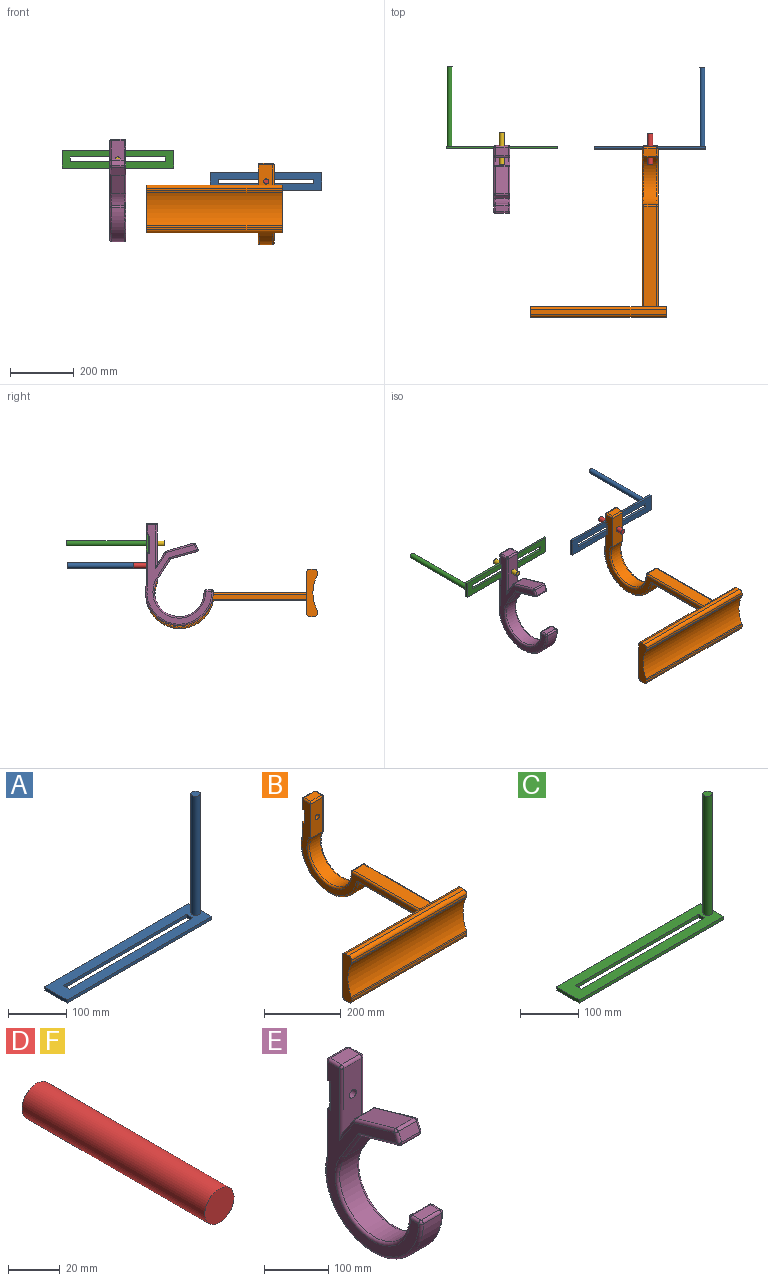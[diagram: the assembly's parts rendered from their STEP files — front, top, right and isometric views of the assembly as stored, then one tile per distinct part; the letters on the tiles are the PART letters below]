
ASSEMBLY  parts=6 mates=4
PART A: 12 faces, bbox 350x54.6x256.5 mm
  f0: plane 350x54.58mm, normal (0,0,1), area 14418.2mm2, adj f1,f3,f4,f5,f6,f7,f8,f9
  f1: plane 350x6.45mm, normal (0,-1,0), area 2257.7mm2, adj f0,f2,f4,f5
  f2: plane 350x54.58mm, normal (0,0,-1), area 14619.2mm2, adj f1,f3,f4,f5,f6,f7,f8,f9
  f3: plane 350x6.45mm, normal (0,1,0), area 2257.7mm2, adj f0,f2,f4,f5
  f4: plane 54.58x6.45mm, normal (1,0,0), area 352.1mm2, adj f0,f1,f2,f3
  f5: plane 54.58x6.45mm, normal (-1,0,0), area 352.1mm2, adj f0,f1,f2,f3
  f6: plane 15x6.45mm, normal (1,0,0), area 96.8mm2, adj f0,f2,f7,f9
  f7: plane 298.97x6.45mm, normal (0,1,0), area 1928.6mm2, adj f0,f2,f6,f8
  f8: plane 15x6.45mm, normal (-1,0,0), area 96.8mm2, adj f0,f2,f7,f9
  f9: plane 298.97x6.45mm, normal (0,-1,0), area 1928.6mm2, adj f0,f2,f6,f8
  f10: cylinder r=8mm len=250mm, axis (0,0,-1), area 12566.4mm2, adj f0,f11
  f11: plane 16x16mm, normal (0,0,1), area 201.1mm2, adj f10
PART B: 68 faces, bbox 425x547.6x264.4 mm
  f0: plane 41.08x40mm, normal (0,1,0), area 1643.3mm2, adj f29,f36,f40,f42
  f1: plane 500.7x245.65mm, normal (-1,0,0), area 13483.1mm2, adj f11,f25,f26,f28,f29,f33,f37,f39
  f2: plane 500.7x245.65mm, normal (1,0,0), area 12934.7mm2, adj f11,f25,f28,f29,f31,f32,f35,f36
  f3: cylinder r=7.5mm len=27.51mm, axis (0,-1,0), area 1296.5mm2, adj f26,f30
  f4: plane 425x7.79mm, normal (0,-1,0), area 3309mm2, adj f13,f16,f19,f22
  f5: plane 290x40mm, normal (0,0,-1), area 11600mm2, adj f11,f31,f33,f34
  f6: plane 316.33x40mm, normal (0,0,1), area 12653.2mm2, adj f11,f44,f50,f51
  f7: cylinder r=106.68mm len=210.82mm, axis (-1,0,0), area 13645.9mm2, adj f34,f35,f39,f40
  f8: cylinder r=77.9mm len=155.57mm, axis (-1,0,0), area 10978.7mm2, adj f10,f43,f48,f49
  f9: plane 40x6.31mm, normal (0,1,0), area 252.3mm2, adj f45,f48,f51,f54
  f10: plane 42.72x0.17mm, normal (0,-0.55,0.83), area 7.8mm2, adj f8,f25,f43,f49
  f11: plane 425x130mm, normal (0,1,0), area 54021.5mm2, adj f1,f2,f5,f6,f13,f16,f21,f23
  f12: plane 425x7.79mm, normal (0,-1,0), area 3309mm2, adj f13,f16,f18,f20
  f13: plane 150x33.08mm, normal (-1,0,0), area 3853.4mm2, adj f4,f11,f12,f14,f15,f17,f18,f19
  f14: plane 425x13.08mm, normal (0,0,1), area 5558.4mm2, adj f13,f16,f22,f23
  f15: plane 425x13.08mm, normal (0,0,-1), area 5558.4mm2, adj f13,f16,f20,f21
  f16: plane 150x33.08mm, normal (1,0,0), area 3853.4mm2, adj f4,f11,f12,f14,f15,f17,f18,f19
  f17: cylinder r=115.34mm len=425mm, axis (1,0,0), area 46473mm2, adj f13,f16,f18,f19
  f18: cylinder r=10mm len=425mm, axis (1,0,0), area 2014.7mm2, adj f12,f13,f16,f17
  f19: cylinder r=10mm len=425mm, axis (1,0,0), area 2014.7mm2, adj f4,f13,f16,f17
  f20: cylinder r=10mm len=425mm, axis (-1,0,0), area 6675.9mm2, adj f12,f13,f15,f16
  f21: cylinder r=10mm len=425mm, axis (1,0,0), area 6675.9mm2, adj f11,f13,f15,f16
  f22: cylinder r=10mm len=425mm, axis (1,0,0), area 6675.9mm2, adj f4,f13,f14,f16
  f23: cylinder r=10mm len=425mm, axis (-1,0,0), area 6675.9mm2, adj f11,f13,f14,f16
  f24: plane 40x26.99mm, normal (0,1,0), area 1079.5mm2, adj f56,f57,f59,f60
  f25: plane 50x6.79mm, normal (0,-0.18,-0.98), area 55.4mm2, adj f1,f2,f10,f26,f43,f49,f65
  f26: plane 109.23x45mm, normal (0,-1,0), area 4738.7mm2, adj f1,f3,f25,f63,f65
  f27: plane 40x23.43mm, normal (0,0,1), area 937.2mm2, adj f55,f60,f62,f63
  f28: plane 50x5.92mm, normal (0,0,-1), area 56.6mm2, adj f1,f2,f30,f57,f66,f67
  f29: plane 50x10.92mm, normal (0,0,1), area 295.9mm2, adj f0,f1,f2,f30,f36,f42,f66,f67
  f30: plane 40.56x40mm, normal (0,1,0), area 1445.7mm2, adj f3,f28,f29,f66,f67
  f31: cylinder r=5mm len=290mm, axis (0,-1,0), area 2277.7mm2, adj f2,f5,f11,f32
  f32: torus R=10mm, axis (1,0,0), area 72.4mm2, adj f2,f31,f34,f35
  f33: cylinder r=5mm len=290mm, axis (0,1,0), area 2277.7mm2, adj f1,f5,f11,f37
  f34: cylinder r=5mm len=40mm, axis (-1,0,0), area 270.4mm2, adj f5,f7,f32,f37
  f35: torus R=101.68mm, axis (1,0,0), area 2633.7mm2, adj f2,f7,f32,f38
  f36: cylinder r=5mm len=41.08mm, axis (0,0,-1), area 322.7mm2, adj f0,f2,f29,f38
  f37: torus R=10mm, axis (1,0,0), area 72.4mm2, adj f1,f33,f34,f39
  f38: torus R=10mm, axis (1,0,0), area 14.7mm2, adj f2,f35,f36,f40
  f39: torus R=101.68mm, axis (1,0,0), area 2633.7mm2, adj f1,f7,f37,f41
  f40: cylinder r=5mm len=40mm, axis (-1,0,0), area 55mm2, adj f0,f7,f38,f41
  f41: torus R=10mm, axis (1,0,0), area 14.7mm2, adj f1,f39,f40,f42
  f42: cylinder r=5mm len=41.08mm, axis (0,0,1), area 322.7mm2, adj f0,f1,f29,f41
  f43: torus R=82.9mm, axis (1,0,0), area 2196.5mm2, adj f1,f8,f10,f25,f46
  f44: cylinder r=5mm len=316.33mm, axis (0,-1,0), area 2484.5mm2, adj f1,f6,f11,f47
  f45: cylinder r=5mm len=6.31mm, axis (0,0,-1), area 49.5mm2, adj f1,f9,f46,f47
  f46: torus R=10mm, axis (1,0,0), area 4.1mm2, adj f1,f43,f45,f48
  f47: sphere r=5mm, area 39.3mm2, adj f44,f45,f51
  f48: cylinder r=5mm len=40mm, axis (-1,0,0), area 15.3mm2, adj f8,f9,f46,f52
  f49: torus R=82.9mm, axis (1,0,0), area 2196.5mm2, adj f2,f8,f10,f25,f52
  f50: cylinder r=5mm len=316.33mm, axis (0,1,0), area 2484.5mm2, adj f2,f6,f11,f53
  f51: cylinder r=5mm len=40mm, axis (-1,0,0), area 314.2mm2, adj f6,f9,f47,f53
  f52: torus R=10mm, axis (1,0,0), area 4.1mm2, adj f2,f48,f49,f54
  f53: sphere r=5mm, area 39.3mm2, adj f50,f51,f54
  f54: cylinder r=5mm len=6.31mm, axis (0,0,1), area 49.5mm2, adj f2,f9,f52,f53
  f55: cylinder r=5mm len=23.43mm, axis (0,1,0), area 184mm2, adj f2,f27,f58,f64
  f56: cylinder r=5mm len=31.99mm, axis (0,0,-1), area 237mm2, adj f2,f24,f57,f58
  f57: cylinder r=5mm len=50mm, axis (1,0,0), area 364.2mm2, adj f24,f28,f56,f59
  f58: sphere r=5mm, area 39.3mm2, adj f55,f56,f60
  f59: cylinder r=5mm len=31.99mm, axis (0,0,1), area 237mm2, adj f1,f24,f57,f61
  f60: cylinder r=5mm len=40mm, axis (-1,0,0), area 314.2mm2, adj f24,f27,f58,f61
  f61: sphere r=5mm, area 39.3mm2, adj f59,f60,f62
  f62: cylinder r=5mm len=28.43mm, axis (0,-1,0), area 209mm2, adj f1,f27,f61,f63
  f63: cylinder r=5mm len=45mm, axis (-1,0,0), area 339.2mm2, adj f26,f27,f62,f64
  f64: sphere r=5mm, area 39.3mm2, adj f55,f63,f65
  f65: cylinder r=5mm len=110.15mm, axis (0,0,1), area 860.5mm2, adj f2,f25,f26,f64
  f66: cylinder r=5mm len=40.56mm, axis (0,0,-1), area 318.6mm2, adj f1,f28,f29,f30
  f67: cylinder r=5mm len=40.56mm, axis (0,0,1), area 318.6mm2, adj f2,f28,f29,f30
PART C: 12 faces, bbox 350x54.6x256.5 mm
  f0: plane 350x54.58mm, normal (0,0,1), area 14418.2mm2, adj f1,f3,f4,f5,f6,f7,f8,f9
  f1: plane 350x6.45mm, normal (0,-1,0), area 2257.7mm2, adj f0,f2,f4,f5
  f2: plane 350x54.58mm, normal (0,0,-1), area 14619.2mm2, adj f1,f3,f4,f5,f6,f7,f8,f9
  f3: plane 350x6.45mm, normal (0,1,0), area 2257.7mm2, adj f0,f2,f4,f5
  f4: plane 54.58x6.45mm, normal (1,0,0), area 352.1mm2, adj f0,f1,f2,f3
  f5: plane 54.58x6.45mm, normal (-1,0,0), area 352.1mm2, adj f0,f1,f2,f3
  f6: plane 15x6.45mm, normal (1,0,0), area 96.8mm2, adj f0,f2,f7,f9
  f7: plane 298.97x6.45mm, normal (0,1,0), area 1928.6mm2, adj f0,f2,f6,f8
  f8: plane 15x6.45mm, normal (-1,0,0), area 96.8mm2, adj f0,f2,f7,f9
  f9: plane 298.97x6.45mm, normal (0,-1,0), area 1928.6mm2, adj f0,f2,f6,f8
  f10: cylinder r=8mm len=250mm, axis (0,0,-1), area 12566.4mm2, adj f0,f11
  f11: plane 16x16mm, normal (0,0,1), area 201.1mm2, adj f10
PART D: 3 faces, bbox 16x100x16 mm
  f0: cylinder r=8mm len=100mm, axis (0,1,0), area 5026.5mm2, adj f1,f2
  f1: plane 16x16mm, normal (0,-1,0), area 201.1mm2, adj f0
  f2: plane 16x16mm, normal (0,1,0), area 201.1mm2, adj f0
PART E: 70 faces, bbox 50x230.9x330.6 mm
  f0: plane 40x37.03mm, normal (0,0.83,0.55), area 1774.7mm2, adj f10,f49,f58,f59
  f1: cylinder r=77.9mm len=155.8mm, axis (1,0,0), area 11671.8mm2, adj f2,f30,f34,f35
  f2: plane 59.19x40mm, normal (0,-0.85,-0.52), area 2775.1mm2, adj f1,f3,f36,f37
  f3: plane 84.21x40mm, normal (0,-0.27,-0.96), area 3493.8mm2, adj f2,f38,f39,f40
  f4: plane 40x17.16mm, normal (0,-0.92,0.39), area 746.8mm2, adj f39,f43,f44,f45
  f5: plane 87.2x40mm, normal (0,0.27,0.96), area 3626.1mm2, adj f44,f48,f49,f50
  f6: cylinder r=106.68mm len=213.37mm, axis (1,0,0), area 14418.3mm2, adj f20,f24,f25,f26
  f7: plane 40x18.78mm, normal (0,0,1), area 751.3mm2, adj f25,f29,f30,f31
  f8: plane 311.77x203.37mm, normal (-1,0,0), area 13032.6mm2, adj f13,f15,f21,f23,f26,f31,f35,f37
  f9: plane 311.77x203.37mm, normal (1,0,0), area 13032.6mm2, adj f13,f15,f19,f22,f24,f29,f34,f36
  f10: plane 121.11x40mm, normal (0,-1,0), area 4667.7mm2, adj f0,f17,f62,f63,f67
  f11: plane 40x25.17mm, normal (0,0,1), area 1006.8mm2, adj f56,f61,f64,f67
  f12: plane 40x30.08mm, normal (0,1,0), area 1203.4mm2, adj f51,f52,f55,f56
  f13: plane 50x6.45mm, normal (0,0,-1), area 83.2mm2, adj f8,f9,f14,f51,f68,f69
  f14: plane 54.58x40mm, normal (0,1,0), area 2006.5mm2, adj f13,f15,f17,f68,f69
  f15: plane 50x6.45mm, normal (0,0,1), area 83.2mm2, adj f8,f9,f14,f18,f68,f69
  f16: plane 89.98x40mm, normal (0,1,0), area 3599.1mm2, adj f18,f19,f20,f21
  f17: cylinder r=7.5mm len=28.72mm, axis (0,-1,0), area 1353.3mm2, adj f10,f14
  f18: cylinder r=5mm len=50mm, axis (-1,0,0), area 364.2mm2, adj f15,f16,f19,f21
  f19: cylinder r=5mm len=94.98mm, axis (0,0,-1), area 731.7mm2, adj f9,f16,f18,f22
  f20: cylinder r=5mm len=40mm, axis (1,0,0), area 46mm2, adj f6,f16,f22,f23
  f21: cylinder r=5mm len=94.98mm, axis (0,0,1), area 731.7mm2, adj f8,f16,f18,f23
  f22: torus R=10mm, axis (1,0,0), area 12.3mm2, adj f9,f19,f20,f24
  f23: torus R=10mm, axis (1,0,0), area 12.3mm2, adj f8,f20,f21,f26
  f24: torus R=101.68mm, axis (1,0,0), area 2782.8mm2, adj f6,f9,f22,f27
  f25: cylinder r=5mm len=40mm, axis (1,0,0), area 312.7mm2, adj f6,f7,f27,f28
  f26: torus R=101.68mm, axis (1,0,0), area 2782.8mm2, adj f6,f8,f23,f28
  f27: sphere r=5mm, area 39.1mm2, adj f24,f25,f29
  f28: sphere r=5mm, area 39.1mm2, adj f25,f26,f31
  f29: cylinder r=5mm len=18.78mm, axis (0,-1,0), area 147.5mm2, adj f7,f9,f27,f32
  f30: cylinder r=5mm len=40mm, axis (1,0,0), area 316mm2, adj f1,f7,f32,f33
  f31: cylinder r=5mm len=18.78mm, axis (0,1,0), area 147.5mm2, adj f7,f8,f28,f33
  f32: sphere r=5mm, area 39.5mm2, adj f29,f30,f34
  f33: sphere r=5mm, area 39.4mm2, adj f30,f31,f35
  f34: torus R=82.9mm, axis (1,0,0), area 2344.8mm2, adj f1,f9,f32,f36
  f35: torus R=82.9mm, axis (1,0,0), area 2344.8mm2, adj f1,f8,f33,f37
  f36: cylinder r=5mm len=63.48mm, axis (0,0.52,-0.85), area 550.1mm2, adj f2,f9,f34,f38
  f37: cylinder r=5mm len=63.48mm, axis (0,-0.52,0.85), area 550.1mm2, adj f2,f8,f35,f40
  f38: cylinder r=5mm len=87.45mm, axis (0,0.96,-0.27), area 691.7mm2, adj f3,f9,f36,f41
  f39: cylinder r=5mm len=40mm, axis (1,0,0), area 341.4mm2, adj f3,f4,f41,f42
  f40: cylinder r=5mm len=87.45mm, axis (0,-0.96,0.27), area 691.7mm2, adj f3,f8,f37,f42
  f41: sphere r=5mm, area 42.7mm2, adj f38,f39,f43
  f42: sphere r=5mm, area 42.7mm2, adj f39,f40,f45
  f43: cylinder r=5mm len=19.13mm, axis (0,-0.39,-0.92), area 146.6mm2, adj f4,f9,f41,f46
  f44: cylinder r=5mm len=40mm, axis (1,0,0), area 288.6mm2, adj f4,f5,f46,f47
  f45: cylinder r=5mm len=19.13mm, axis (0,0.39,0.92), area 146.6mm2, adj f4,f8,f42,f47
  f46: sphere r=5mm, area 36.1mm2, adj f43,f44,f48
  f47: sphere r=5mm, area 36.1mm2, adj f44,f45,f50
  f48: cylinder r=5mm len=88.57mm, axis (0,-0.96,0.27), area 712mm2, adj f5,f9,f46,f53
  f49: cylinder r=5mm len=40mm, axis (1,0,0), area 142.2mm2, adj f0,f5,f53,f54
  f50: cylinder r=5mm len=88.57mm, axis (0,0.96,-0.27), area 712mm2, adj f5,f8,f47,f54
  f51: cylinder r=5mm len=50mm, axis (-1,0,0), area 364.2mm2, adj f12,f13,f52,f55
  f52: cylinder r=5mm len=35.08mm, axis (0,0,-1), area 261.3mm2, adj f9,f12,f51,f57
  f53: sphere r=5mm, area 17.8mm2, adj f48,f49,f58
  f54: sphere r=5mm, area 17.8mm2, adj f49,f50,f59
  f55: cylinder r=5mm len=35.08mm, axis (0,0,1), area 261.3mm2, adj f8,f12,f51,f60
  f56: cylinder r=5mm len=40mm, axis (-1,0,0), area 314.2mm2, adj f11,f12,f57,f60
  f57: sphere r=5mm, area 39.3mm2, adj f52,f56,f61
  f58: cylinder r=5mm len=53.69mm, axis (0,-0.55,0.83), area 396mm2, adj f0,f9,f53,f62
  f59: cylinder r=5mm len=53.69mm, axis (0,0.55,-0.83), area 396mm2, adj f0,f8,f54,f63
  f60: sphere r=5mm, area 39.3mm2, adj f55,f56,f64
  f61: cylinder r=5mm len=25.17mm, axis (0,1,0), area 197.7mm2, adj f9,f11,f57,f65
  f62: cylinder r=5mm len=137.77mm, axis (0,0,1), area 998.7mm2, adj f9,f10,f58,f65
  f63: cylinder r=5mm len=137.77mm, axis (0,0,-1), area 998.7mm2, adj f8,f10,f59,f66
  f64: cylinder r=5mm len=25.17mm, axis (0,-1,0), area 197.7mm2, adj f8,f11,f60,f66
  f65: sphere r=5mm, area 39.3mm2, adj f61,f62,f67
  f66: sphere r=5mm, area 39.3mm2, adj f63,f64,f67
  f67: cylinder r=5mm len=40mm, axis (-1,0,0), area 314.2mm2, adj f10,f11,f65,f66
  f68: cylinder r=5mm len=54.58mm, axis (0,0,1), area 428.7mm2, adj f8,f13,f14,f15
  f69: cylinder r=5mm len=54.58mm, axis (0,0,-1), area 428.7mm2, adj f9,f13,f14,f15
PART F: same geometry as D
PLACE A rot(axis=(-1,0,0),90deg) t=(-641.28,70.64,-139.06)mm
PLACE B t=(-691.28,-116.65,-1642.74)mm
PLACE C rot(axis=(0,0.71,0.71),180deg) t=(-581.23,369.72,-42.42)mm
PLACE D rot(axis=(1,0,0),0deg) t=(-425.93,116.25,-150.55)mm
PLACE E t=(-697.23,-115.29,-1633.42)mm
PLACE F t=(-891.88,118.34,-81.05)mm
MATE fastened A.f2 <-> D.f0  axis (0,-1,0) through (-466.28,66.25,-125.49)mm
MATE fastened F.f0 <-> E.f17  axis (0,1,0) through (-932.23,68.34,-55.99)mm
MATE fastened D.f0 <-> B.f3  axis (0,1,0) through (-466.28,66.25,-125.49)mm
MATE fastened C.f2 <-> F.f0  axis (0,-1,0) through (-932.23,68.34,-55.99)mm
